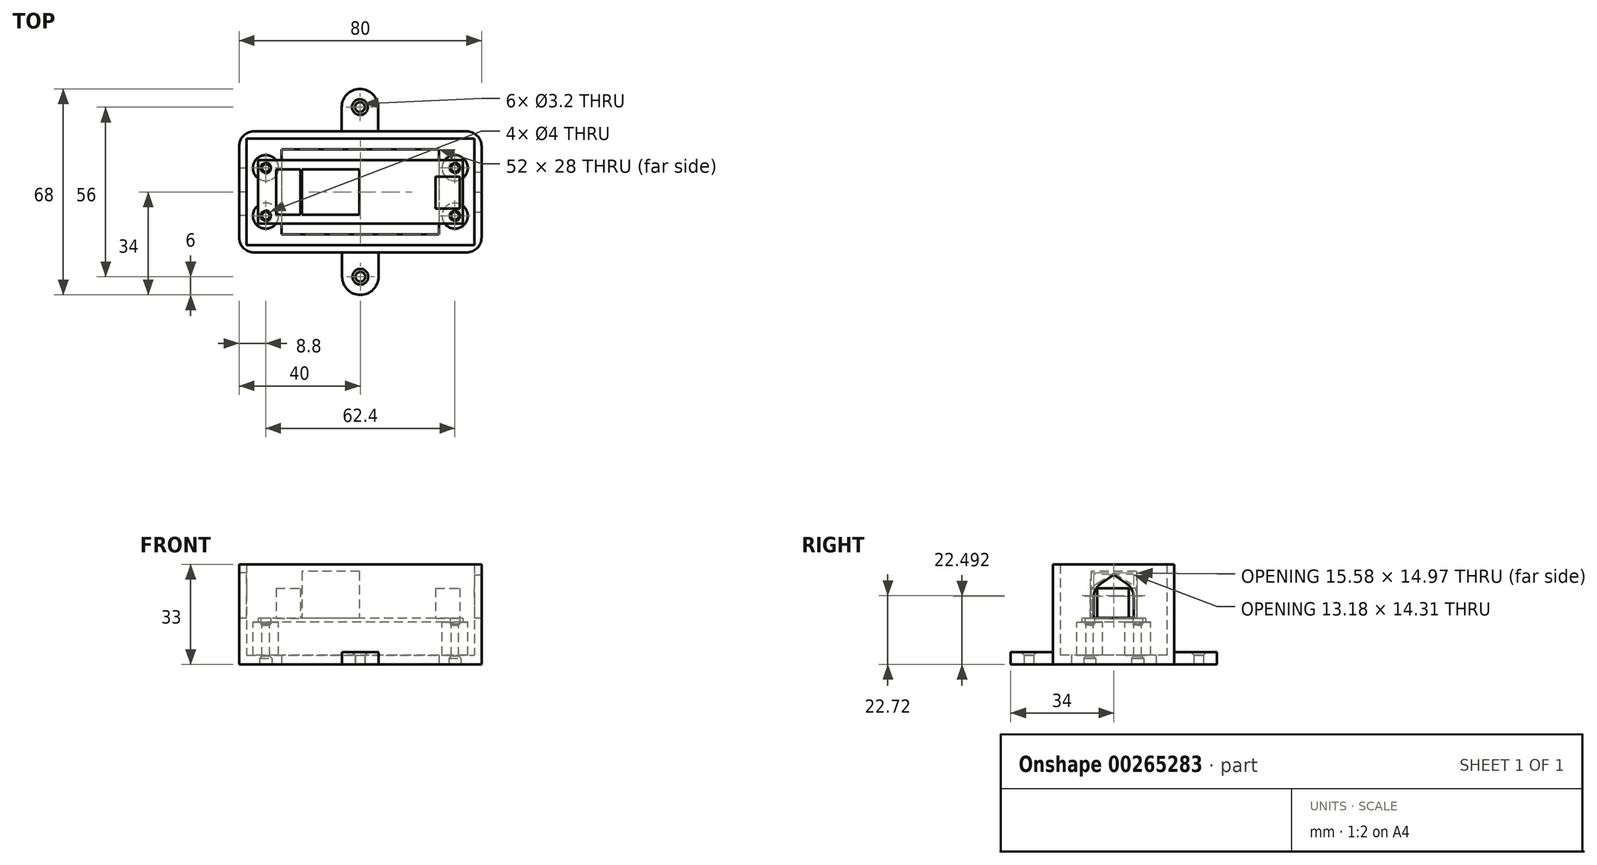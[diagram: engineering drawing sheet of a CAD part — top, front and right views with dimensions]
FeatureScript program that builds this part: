
annotation { "Feature Type Name" : "Feature", "Feature Type Description" : "" }
export const myFeature = defineFeature(function(context is Context, id is Id, definition is map)
    precondition{}
    {
        {
            var Q0;
            Q0=qCreatedBy(makeId("Top.planeOp"),FACE);
            cPlane(context, id + "F0", {"entities" : qUnion([Q0]), "cplaneType" : CPlaneType.OFFSET, "offset" : 14 * mm, "oppositeDirection" : true, "width" : 150 * mm, "height" : 150 * mm});
        }
        {
            var Q0;
            Q0=qCreatedBy(makeId("Top.planeOp"),FACE);
            var sketch = newSketch(context, id + "F1", { "sketchPlane" : qUnion([Q0])});
            skLineSegment(sketch, "E0.bottom", {"start": v(33.8, 10.5) * mm, "end": v(-33.8, 10.5) * mm});
            skLineSegment(sketch, "E0.top", {"start": v(33.8, -10.5) * mm, "end": v(-33.8, -10.5) * mm});
            skLineSegment(sketch, "E0.left", {"start": v(33.8, 10.5) * mm, "end": v(33.8, -10.5) * mm});
            skLineSegment(sketch, "E0.right", {"start": v(-33.8, 10.5) * mm, "end": v(-33.8, -10.5) * mm});
            skPoint(sketch, "E0.middle", {"position": v(0, 0) * mm});
            skCircle(sketch, "E1", {"center": v(-31.2, 7.9) * mm, "radius": 1.6 * mm});
            skCircle(sketch, "E2", {"center": v(31.2, 7.9) * mm, "radius": 1.6 * mm});
            skCircle(sketch, "E3", {"center": v(-31.2, -7.9) * mm, "radius": 1.6 * mm});
            skCircle(sketch, "E4", {"center": v(31.2, -7.9) * mm, "radius": 1.6 * mm});
            skSolve(sketch);
        }
        {
            var Q0;
            Q0 = qSketchRegion(id + "F1", true);
            extrude(context, id + "F2", {"entities" : qUnion([Q0]), "depth" : 1.2 * mm});
        }
        {
            var Q0;
            Q0=qCreatedBy(id+"F0.planeOp",FACE);
            var sketch = newSketch(context, id + "F3", { "sketchPlane" : qUnion([Q0])});
            skLineSegment(sketch, "E5.bottom", {"start": v(-40, 20) * mm, "end": v(40, 20) * mm});
            skLineSegment(sketch, "E5.top", {"start": v(-40, -20) * mm, "end": v(40, -20) * mm});
            skLineSegment(sketch, "E5.left", {"start": v(-40, 20) * mm, "end": v(-40, -20) * mm});
            skLineSegment(sketch, "E5.right", {"start": v(40, 20) * mm, "end": v(40, -20) * mm});
            skPoint(sketch, "E5.middle", {"position": v(0, 0) * mm});
            skLineSegment(sketch, "E6.bottom", {"start": v(26, 14) * mm, "end": v(-26, 14) * mm});
            skLineSegment(sketch, "E6.top", {"start": v(26, -14) * mm, "end": v(-26, -14) * mm});
            skLineSegment(sketch, "E6.left", {"start": v(26, 14) * mm, "end": v(26, -14) * mm});
            skLineSegment(sketch, "E6.right", {"start": v(-26, 14) * mm, "end": v(-26, -14) * mm});
            skSolve(sketch);
        }
        {
            var Q0;
            Q0 = qSketchRegion(id + "F3", true);
            extrude(context, id + "F4", {"entities" : qUnion([Q0]), "depth" : 3 * mm});
        }
        {
            var Q0;
            Q0=makeQuery(id+"F2.opExtrude","CAP_FACE",FACE,{"disambiguationData":[OSD([sQuery(id+"F1.wireOp",EDGE,"E0.bottom"),sQuery(id+"F1.wireOp",EDGE,"E0.top"),sQuery(id+"F1.wireOp",EDGE,"E0.left"),sQuery(id+"F1.wireOp",EDGE,"E0.right"),sQuery(id+"F1.wireOp",EDGE,"E1"),sQuery(id+"F1.wireOp",EDGE,"E2"),sQuery(id+"F1.wireOp",EDGE,"E3"),sQuery(id+"F1.wireOp",EDGE,"E4")])],"isStart":true});
            var sketch = newSketch(context, id + "F5", { "sketchPlane" : qUnion([Q0])});
            skCircle(sketch, "E7", {"center": v(-31.2, 7.9) * mm, "radius": 1.25 * mm});
            skCircle(sketch, "E8", {"center": v(-31.2, 7.9) * mm, "radius": 4.25 * mm});
            skCircle(sketch, "E9", {"center": v(-31.2, -7.9) * mm, "radius": 1.25 * mm});
            skCircle(sketch, "E10", {"center": v(-31.2, -7.9) * mm, "radius": 4.25 * mm});
            skCircle(sketch, "E11", {"center": v(31.2, 7.9) * mm, "radius": 1.25 * mm});
            skCircle(sketch, "E12", {"center": v(31.2, 7.9) * mm, "radius": 4.25 * mm});
            skCircle(sketch, "E13", {"center": v(31.2, -7.9) * mm, "radius": 1.25 * mm});
            skCircle(sketch, "E14", {"center": v(31.2, -7.9) * mm, "radius": 4.25 * mm});
            skSolve(sketch);
        }
        {
            var Q0;
            Q0 = qSketchRegion(id + "F5", true);
            extrude(context, id + "F6", {"entities" : qUnion([Q0]), "operationType" : NewBodyOperationType.ADD, "depth" : 14 * mm});
        }
        {
            var Q0;
            Q0=makeQuery(id+"F2.opExtrude","CAP_FACE",FACE,{"disambiguationData":[OSD([sQuery(id+"F1.wireOp",EDGE,"E0.bottom"),sQuery(id+"F1.wireOp",EDGE,"E0.top"),sQuery(id+"F1.wireOp",EDGE,"E0.left"),sQuery(id+"F1.wireOp",EDGE,"E0.right"),sQuery(id+"F1.wireOp",EDGE,"E1"),sQuery(id+"F1.wireOp",EDGE,"E2"),sQuery(id+"F1.wireOp",EDGE,"E3"),sQuery(id+"F1.wireOp",EDGE,"E4")])],"isStart":false});
            var sketch = newSketch(context, id + "F7", { "sketchPlane" : qUnion([Q0])});
            skLineSegment(sketch, "E15.bottom", {"start": v(-27.8, 7.5) * mm, "end": v(-19.8, 7.5) * mm});
            skLineSegment(sketch, "E15.top", {"start": v(-27.8, -7.5) * mm, "end": v(-19.8, -7.5) * mm});
            skLineSegment(sketch, "E15.left", {"start": v(-27.8, 7.5) * mm, "end": v(-27.8, -7.5) * mm});
            skLineSegment(sketch, "E15.right", {"start": v(-19.8, 7.5) * mm, "end": v(-19.8, -7.5) * mm});
            skLineSegment(sketch, "E16.bottom", {"start": v(24.8, 5) * mm, "end": v(32.8, 5) * mm});
            skLineSegment(sketch, "E16.top", {"start": v(24.8, -5.5) * mm, "end": v(32.8, -5.5) * mm});
            skLineSegment(sketch, "E16.left", {"start": v(24.8, 5) * mm, "end": v(24.8, -5.5) * mm});
            skLineSegment(sketch, "E16.right", {"start": v(32.8, 5) * mm, "end": v(32.8, -5.5) * mm});
            skSolve(sketch);
        }
        {
            var Q0;
            Q0 = qSketchRegion(id + "F7", true);
            extrude(context, id + "F8", {"entities" : qUnion([Q0]), "operationType" : NewBodyOperationType.ADD, "depth" : 10 * mm});
        }
        {
            var Q0;
            Q0=makeQuery(id+"F2.opExtrude","CAP_FACE",FACE,{"disambiguationData":[OSD([sQuery(id+"F1.wireOp",EDGE,"E0.bottom"),sQuery(id+"F1.wireOp",EDGE,"E0.top"),sQuery(id+"F1.wireOp",EDGE,"E0.left"),sQuery(id+"F1.wireOp",EDGE,"E0.right"),sQuery(id+"F1.wireOp",EDGE,"E1"),sQuery(id+"F1.wireOp",EDGE,"E2"),sQuery(id+"F1.wireOp",EDGE,"E3"),sQuery(id+"F1.wireOp",EDGE,"E4")])],"isStart":false});
            var sketch = newSketch(context, id + "F9", { "sketchPlane" : qUnion([Q0])});
            skLineSegment(sketch, "E17.bottom", {"start": v(-0.3, 7.5) * mm, "end": v(-19.3, 7.5) * mm});
            skLineSegment(sketch, "E17.top", {"start": v(-0.3, -7.5) * mm, "end": v(-19.3, -7.5) * mm});
            skLineSegment(sketch, "E17.left", {"start": v(-0.3, 7.5) * mm, "end": v(-0.3, -7.5) * mm});
            skLineSegment(sketch, "E17.right", {"start": v(-19.3, 7.5) * mm, "end": v(-19.3, -7.5) * mm});
            skSolve(sketch);
        }
        {
            var Q0;
            Q0 = qSketchRegion(id + "F9", true);
            extrude(context, id + "F10", {"entities" : qUnion([Q0]), "operationType" : NewBodyOperationType.ADD, "depth" : 15.5 * mm});
        }
        {
            var Q0;
            {var subQ0=sQuery(id+"F3.wireOp",EDGE,"E5.right");var subQ1=sQuery(id+"F3.wireOp",EDGE,"E5.left");var subQ2=sQuery(id+"F3.wireOp",EDGE,"E5.top");var subQ3=sQuery(id+"F3.wireOp",EDGE,"E5.bottom");Q0=makeQuery(id+"F6.boolean.opBoolean","SPLIT",FACE,{"disambiguationData":[TD([makeQuery(id+"F4.opExtrude","SWEPT_FACE",FACE,{"disambiguationData":[OSD([subQ3])]})])],"derivedFrom":makeQuery(id+"F4.opExtrude","CAP_FACE",FACE,{"disambiguationData":[OSD([subQ3,subQ2,subQ1,subQ0])],"isStart":false})});}
            var sketch = newSketch(context, id + "F11", { "sketchPlane" : qUnion([Q0])});
            skLineSegment(sketch, "E18.bottom", {"start": v(-40, 20) * mm, "end": v(40, 20) * mm});
            skLineSegment(sketch, "E18.top", {"start": v(-40, -20) * mm, "end": v(40, -20) * mm});
            skLineSegment(sketch, "E18.left", {"start": v(-40, 20) * mm, "end": v(-40, -20) * mm});
            skLineSegment(sketch, "E18.right", {"start": v(40, 20) * mm, "end": v(40, -20) * mm});
            skPoint(sketch, "E18.middle", {"position": v(0, 0) * mm});
            skLineSegment(sketch, "E19.bottom", {"start": v(-37.6, 17.6) * mm, "end": v(37.6, 17.6) * mm});
            skLineSegment(sketch, "E19.top", {"start": v(-37.6, -17.6) * mm, "end": v(37.6, -17.6) * mm});
            skLineSegment(sketch, "E19.left", {"start": v(-37.6, 17.6) * mm, "end": v(-37.6, -17.6) * mm});
            skLineSegment(sketch, "E19.right", {"start": v(37.6, 17.6) * mm, "end": v(37.6, -17.6) * mm});
            skSolve(sketch);
        }
        {
            var Q0;
            Q0 = qSketchRegion(id + "F11", true);
            extrude(context, id + "F12", {"entities" : qUnion([Q0]), "operationType" : NewBodyOperationType.ADD, "depth" : 30 * mm});
        }
        {
            var Q0;
            Q0=makeQuery(id+"F12.boolean.opBoolean","MERGE",FACE,{"derivedFrom":[makeQuery(id+"F4.opExtrude","SWEPT_FACE",FACE,{"disambiguationData":[OSD([sQuery(id+"F3.wireOp",EDGE,"E5.left")])]}),makeQuery(id+"F12.opExtrude","SWEPT_FACE",FACE,{"disambiguationData":[OSD([sQuery(id+"F11.wireOp",EDGE,"E18.left")])]})]});
            var sketch = newSketch(context, id + "F13", { "sketchPlane" : qUnion([Q0])});
            skLineSegment(sketch, "E20.bottom", {"start": v(7.79, 1.23) * mm, "end": v(-7.79, 1.23) * mm});
            skLineSegment(sketch, "E20.left", {"start": v(7.79, 1.23) * mm, "end": v(7.79, 11.29) * mm});
            skLineSegment(sketch, "E20.right", {"start": v(-7.79, 1.23) * mm, "end": v(-7.79, 11.29) * mm});
            skPoint(sketch, "E20.middle", {"position": v(0, 6.26) * mm});
            skLineSegment(sketch, "E21", {"start": v(7.79, 11.29) * mm, "end": v(0, 16.2) * mm});
            skLineSegment(sketch, "E22", {"start": v(0, 16.2) * mm, "end": v(-7.79, 11.29) * mm});
            skSolve(sketch);
        }
        {
            var Q0;
            Q0 = qSketchRegion(id + "F13", true);
            var Q1;
            Q1=makeQuery(id+"F12.opExtrude","SWEPT_FACE",FACE,{"disambiguationData":[OSD([sQuery(id+"F11.wireOp",EDGE,"E19.left")])]});
            extrude(context, id + "F14", {"entities" : qUnion([Q0]), "operationType" : NewBodyOperationType.REMOVE, "endBound" : BoundingType.UP_TO_SURFACE, "oppositeDirection" : true, "endBoundEntityFace" : qUnion([Q1]), "depth" : 25 * mm});
        }
        {
            var Q0;
            Q0=makeQuery(id+"F12.boolean.opBoolean","MERGE",FACE,{"derivedFrom":[makeQuery(id+"F4.opExtrude","SWEPT_FACE",FACE,{"disambiguationData":[OSD([sQuery(id+"F3.wireOp",EDGE,"E5.right")])]}),makeQuery(id+"F12.opExtrude","SWEPT_FACE",FACE,{"disambiguationData":[OSD([sQuery(id+"F11.wireOp",EDGE,"E18.right")])]})]});
            var sketch = newSketch(context, id + "F15", { "sketchPlane" : qUnion([Q0])});
            skLineSegment(sketch, "E23.bottom", {"start": v(6.6, 1.33) * mm, "end": v(-6.6, 1.33) * mm});
            skLineSegment(sketch, "E23.left", {"start": v(6.6, 1.33) * mm, "end": v(6.6, 10.98) * mm});
            skLineSegment(sketch, "E23.right", {"start": v(-6.6, 1.33) * mm, "end": v(-6.6, 10.98) * mm});
            skPoint(sketch, "E23.middle", {"position": v(0, 6.16) * mm});
            skLineSegment(sketch, "E24", {"start": v(6.6, 10.98) * mm, "end": v(0, 15.65) * mm});
            skLineSegment(sketch, "E25", {"start": v(0, 15.65) * mm, "end": v(-6.6, 10.98) * mm});
            skSolve(sketch);
        }
        {
            var Q0;
            Q0 = qSketchRegion(id + "F15", true);
            var Q1;
            Q1=makeQuery(id+"F12.opExtrude","SWEPT_FACE",FACE,{"disambiguationData":[OSD([sQuery(id+"F11.wireOp",EDGE,"E19.right")])]});
            extrude(context, id + "F16", {"entities" : qUnion([Q0]), "operationType" : NewBodyOperationType.REMOVE, "endBound" : BoundingType.UP_TO_SURFACE, "oppositeDirection" : true, "endBoundEntityFace" : qUnion([Q1]), "depth" : 25 * mm});
        }
        {
            var Q0;
            Q0=makeQuery(id+"F16.boolean.opBoolean","COPY",EDGE,{"derivedFrom":makeQuery(id+"F16.opExtrude","SWEPT_EDGE",EDGE,{"disambiguationData":[OSD([sQuery(id+"F15.wireOp",EDGE,"E23.left"),sQuery(id+"F15.wireOp",EDGE,"E24")])]})});
            var Q1;
            Q1=makeQuery(id+"F14.boolean.opBoolean","COPY",EDGE,{"derivedFrom":makeQuery(id+"F14.opExtrude","SWEPT_EDGE",EDGE,{"disambiguationData":[OSD([sQuery(id+"F13.wireOp",EDGE,"E20.left"),sQuery(id+"F13.wireOp",EDGE,"E21")])]})});
            var Q2;
            Q2=makeQuery(id+"F14.boolean.opBoolean","COPY",EDGE,{"derivedFrom":makeQuery(id+"F14.opExtrude","SWEPT_EDGE",EDGE,{"disambiguationData":[OSD([sQuery(id+"F13.wireOp",EDGE,"E20.right"),sQuery(id+"F13.wireOp",EDGE,"E22")])]})});
            var Q3;
            Q3=makeQuery(id+"F16.boolean.opBoolean","COPY",EDGE,{"derivedFrom":makeQuery(id+"F16.opExtrude","SWEPT_EDGE",EDGE,{"disambiguationData":[OSD([sQuery(id+"F15.wireOp",EDGE,"E23.right"),sQuery(id+"F15.wireOp",EDGE,"E25")])]})});
            var Q4;
            Q4=makeQuery(id+"F12.boolean.opBoolean","MERGE",EDGE,{"derivedFrom":[makeQuery(id+"F4.opExtrude","SWEPT_EDGE",EDGE,{"disambiguationData":[OSD([sQuery(id+"F3.wireOp",EDGE,"E5.top"),sQuery(id+"F3.wireOp",EDGE,"E5.right")])]}),makeQuery(id+"F12.opExtrude","SWEPT_EDGE",EDGE,{"disambiguationData":[OSD([sQuery(id+"F11.wireOp",EDGE,"E18.top"),sQuery(id+"F11.wireOp",EDGE,"E18.right")])]})]});
            var Q5;
            Q5=makeQuery(id+"F12.boolean.opBoolean","MERGE",EDGE,{"derivedFrom":[makeQuery(id+"F4.opExtrude","SWEPT_EDGE",EDGE,{"disambiguationData":[OSD([sQuery(id+"F3.wireOp",EDGE,"E5.bottom"),sQuery(id+"F3.wireOp",EDGE,"E5.right")])]}),makeQuery(id+"F12.opExtrude","SWEPT_EDGE",EDGE,{"disambiguationData":[OSD([sQuery(id+"F11.wireOp",EDGE,"E18.bottom"),sQuery(id+"F11.wireOp",EDGE,"E18.right")])]})]});
            var Q6;
            Q6=makeQuery(id+"F12.boolean.opBoolean","MERGE",EDGE,{"derivedFrom":[makeQuery(id+"F4.opExtrude","SWEPT_EDGE",EDGE,{"disambiguationData":[OSD([sQuery(id+"F3.wireOp",EDGE,"E5.bottom"),sQuery(id+"F3.wireOp",EDGE,"E5.left")])]}),makeQuery(id+"F12.opExtrude","SWEPT_EDGE",EDGE,{"disambiguationData":[OSD([sQuery(id+"F11.wireOp",EDGE,"E18.bottom"),sQuery(id+"F11.wireOp",EDGE,"E18.left")])]})]});
            var Q7;
            Q7=makeQuery(id+"F12.boolean.opBoolean","MERGE",EDGE,{"derivedFrom":[makeQuery(id+"F4.opExtrude","SWEPT_EDGE",EDGE,{"disambiguationData":[OSD([sQuery(id+"F3.wireOp",EDGE,"E5.top"),sQuery(id+"F3.wireOp",EDGE,"E5.left")])]}),makeQuery(id+"F12.opExtrude","SWEPT_EDGE",EDGE,{"disambiguationData":[OSD([sQuery(id+"F11.wireOp",EDGE,"E18.top"),sQuery(id+"F11.wireOp",EDGE,"E18.left")])]})]});
            fillet(context, id + "F17", {"entities" : qUnion([Q0, Q1, Q2, Q3, Q4, Q5, Q6, Q7]), "radius" : 5 * mm, "tangentPropagation" : true, "allowEdgeOverflow" : false});
        }
        {
            var Q0;
            Q0=makeQuery(id+"F4.opExtrude","CAP_FACE",FACE,{"disambiguationData":[OSD([sQuery(id+"F3.wireOp",EDGE,"E5.bottom"),sQuery(id+"F3.wireOp",EDGE,"E5.top"),sQuery(id+"F3.wireOp",EDGE,"E5.left"),sQuery(id+"F3.wireOp",EDGE,"E5.right"),sQuery(id+"F3.wireOp",EDGE,"E6.bottom"),sQuery(id+"F3.wireOp",EDGE,"E6.top"),sQuery(id+"F3.wireOp",EDGE,"E6.left"),sQuery(id+"F3.wireOp",EDGE,"E6.right")])],"isStart":true});
            var sketch = newSketch(context, id + "F18", { "sketchPlane" : qUnion([Q0])});
            skLineSegment(sketch, "E26.bottom", {"start": v(6, 34) * mm, "end": v(-6, 34) * mm});
            skLineSegment(sketch, "E26.top", {"start": v(6, 20) * mm, "end": v(-6, 20) * mm});
            skLineSegment(sketch, "E26.left", {"start": v(6, 34) * mm, "end": v(6, 20) * mm});
            skLineSegment(sketch, "E26.right", {"start": v(-6, 34) * mm, "end": v(-6, 20) * mm});
            skPoint(sketch, "E26.middle", {"position": v(0, 28) * mm});
            skCircle(sketch, "E27", {"center": v(0, 28) * mm, "radius": 1.6 * mm});
            skLineSegment(sketch, "E28.bottom", {"start": v(5.85, -20) * mm, "end": v(-6.15, -20) * mm});
            skLineSegment(sketch, "E28.top", {"start": v(5.85, -34) * mm, "end": v(-6.15, -34) * mm});
            skLineSegment(sketch, "E28.left", {"start": v(5.85, -20) * mm, "end": v(5.85, -34) * mm});
            skLineSegment(sketch, "E28.right", {"start": v(-6.15, -20) * mm, "end": v(-6.15, -34) * mm});
            skPoint(sketch, "E28.middle", {"position": v(-0.15, -28) * mm});
            skCircle(sketch, "E29", {"center": v(-0.15, -28) * mm, "radius": 1.6 * mm});
            skSolve(sketch);
        }
        {
            var Q0;
            Q0 = qSketchRegion(id + "F18", true);
            extrude(context, id + "F19", {"entities" : qUnion([Q0]), "operationType" : NewBodyOperationType.ADD, "oppositeDirection" : true, "depth" : 4 * mm});
        }
        {
            var Q0;
            Q0=makeQuery(id+"F19.opExtrude","SWEPT_EDGE",EDGE,{"disambiguationData":[OSD([sQuery(id+"F18.wireOp",EDGE,"E26.bottom"),sQuery(id+"F18.wireOp",EDGE,"E26.left")])]});
            var Q1;
            Q1=makeQuery(id+"F19.opExtrude","SWEPT_EDGE",EDGE,{"disambiguationData":[OSD([sQuery(id+"F18.wireOp",EDGE,"E26.bottom"),sQuery(id+"F18.wireOp",EDGE,"E26.right")])]});
            var Q2;
            Q2=makeQuery(id+"F19.opExtrude","SWEPT_EDGE",EDGE,{"disambiguationData":[OSD([sQuery(id+"F18.wireOp",EDGE,"E28.top"),sQuery(id+"F18.wireOp",EDGE,"E28.left")])]});
            var Q3;
            Q3=makeQuery(id+"F19.opExtrude","SWEPT_EDGE",EDGE,{"disambiguationData":[OSD([sQuery(id+"F18.wireOp",EDGE,"E28.top"),sQuery(id+"F18.wireOp",EDGE,"E28.right")])]});
            var Q4;
            Q4=makeQuery(id+"F19.opExtrude","SWEPT_EDGE",EDGE,{"disambiguationData":[OSD([sQuery(id+"F3.wireOp",EDGE,"E5.bottom"),sQuery(id+"F18.wireOp",EDGE,"E28.bottom"),sQuery(id+"F18.wireOp",EDGE,"E28.left")])]});
            var Q5;
            Q5=makeQuery(id+"F19.opExtrude","SWEPT_EDGE",EDGE,{"disambiguationData":[OSD([sQuery(id+"F3.wireOp",EDGE,"E5.bottom"),sQuery(id+"F18.wireOp",EDGE,"E28.bottom"),sQuery(id+"F18.wireOp",EDGE,"E28.right")])]});
            var Q6;
            Q6=makeQuery(id+"F19.opExtrude","SWEPT_EDGE",EDGE,{"disambiguationData":[OSD([sQuery(id+"F3.wireOp",EDGE,"E5.top"),sQuery(id+"F18.wireOp",EDGE,"E26.top"),sQuery(id+"F18.wireOp",EDGE,"E26.left")])]});
            var Q7;
            Q7=makeQuery(id+"F19.opExtrude","SWEPT_EDGE",EDGE,{"disambiguationData":[OSD([sQuery(id+"F3.wireOp",EDGE,"E5.top"),sQuery(id+"F18.wireOp",EDGE,"E26.top"),sQuery(id+"F18.wireOp",EDGE,"E26.right")])]});
            fillet(context, id + "F20", {"entities" : qUnion([Q0, Q1, Q2, Q3, Q4, Q5, Q6, Q7]), "radius" : 6 * mm, "tangentPropagation" : true, "allowEdgeOverflow" : false});
        }
        {
            var Q0;
            Q0=makeQuery(id+"F19.boolean.opBoolean","MERGE",FACE,{"derivedFrom":[makeQuery(id+"F4.opExtrude","CAP_FACE",FACE,{"disambiguationData":[OSD([sQuery(id+"F3.wireOp",EDGE,"E5.bottom"),sQuery(id+"F3.wireOp",EDGE,"E5.top"),sQuery(id+"F3.wireOp",EDGE,"E5.left"),sQuery(id+"F3.wireOp",EDGE,"E5.right"),sQuery(id+"F3.wireOp",EDGE,"E6.bottom"),sQuery(id+"F3.wireOp",EDGE,"E6.top"),sQuery(id+"F3.wireOp",EDGE,"E6.left"),sQuery(id+"F3.wireOp",EDGE,"E6.right")])],"isStart":true}),makeQuery(id+"F19.opExtrude","CAP_FACE",FACE,{"disambiguationData":[OSD([sQuery(id+"F18.wireOp",EDGE,"E26.bottom"),sQuery(id+"F18.wireOp",EDGE,"E26.top"),sQuery(id+"F18.wireOp",EDGE,"E26.left"),sQuery(id+"F18.wireOp",EDGE,"E26.right"),sQuery(id+"F18.wireOp",EDGE,"E27")])],"isStart":true}),makeQuery(id+"F19.opExtrude","CAP_FACE",FACE,{"disambiguationData":[OSD([sQuery(id+"F18.wireOp",EDGE,"E28.bottom"),sQuery(id+"F18.wireOp",EDGE,"E28.top"),sQuery(id+"F18.wireOp",EDGE,"E28.left"),sQuery(id+"F18.wireOp",EDGE,"E28.right"),sQuery(id+"F18.wireOp",EDGE,"E29")])],"isStart":true})]});
            var sketch = newSketch(context, id + "F21", { "sketchPlane" : qUnion([Q0])});
            skCircle(sketch, "E30", {"center": v(-31.2, -7.9) * mm, "radius": 2 * mm});
            skCircle(sketch, "E31", {"center": v(-31.2, 7.9) * mm, "radius": 2 * mm});
            skCircle(sketch, "E32", {"center": v(31.2, -7.9) * mm, "radius": 2 * mm});
            skCircle(sketch, "E33", {"center": v(31.2, 7.9) * mm, "radius": 2 * mm});
            skSolve(sketch);
        }
        {
            var Q0;
            Q0 = qSketchRegion(id + "F21", true);
            extrude(context, id + "F22", {"entities" : qUnion([Q0]), "operationType" : NewBodyOperationType.REMOVE, "oppositeDirection" : true, "depth" : 3 * mm});
        }
        {
            var Q0;
            Q0=makeQuery(id+"F22.boolean.opBoolean","COPY",EDGE,{"derivedFrom":makeQuery(id+"F22.opExtrude","CAP_EDGE",EDGE,{"disambiguationData":[OSD([sQuery(id+"F21.wireOp",EDGE,"E32")])],"isStart":false})});
            var Q1;
            Q1=makeQuery(id+"F22.boolean.opBoolean","COPY",EDGE,{"derivedFrom":makeQuery(id+"F22.opExtrude","CAP_EDGE",EDGE,{"disambiguationData":[OSD([sQuery(id+"F21.wireOp",EDGE,"E33")])],"isStart":false})});
            var Q2;
            Q2=makeQuery(id+"F22.boolean.opBoolean","COPY",EDGE,{"derivedFrom":makeQuery(id+"F22.opExtrude","CAP_EDGE",EDGE,{"disambiguationData":[OSD([sQuery(id+"F21.wireOp",EDGE,"E31")])],"isStart":false})});
            var Q3;
            Q3=makeQuery(id+"F22.boolean.opBoolean","COPY",EDGE,{"derivedFrom":makeQuery(id+"F22.opExtrude","CAP_EDGE",EDGE,{"disambiguationData":[OSD([sQuery(id+"F21.wireOp",EDGE,"E30")])],"isStart":false})});
            var Q4;
            Q4=makeQuery(id+"F6.opExtrude","CAP_EDGE",EDGE,{"disambiguationData":[OSD([sQuery(id+"F5.wireOp",EDGE,"E7")])],"isStart":true});
            var Q5;
            Q5=makeQuery(id+"F6.opExtrude","CAP_EDGE",EDGE,{"disambiguationData":[OSD([sQuery(id+"F5.wireOp",EDGE,"E9")])],"isStart":true});
            var Q6;
            Q6=makeQuery(id+"F6.opExtrude","CAP_EDGE",EDGE,{"disambiguationData":[OSD([sQuery(id+"F5.wireOp",EDGE,"E11")])],"isStart":true});
            var Q7;
            Q7=makeQuery(id+"F6.opExtrude","CAP_EDGE",EDGE,{"disambiguationData":[OSD([sQuery(id+"F5.wireOp",EDGE,"E13")])],"isStart":true});
            var Q8;
            Q8=makeQuery(id+"F19.opExtrude","CAP_EDGE",EDGE,{"disambiguationData":[OSD([sQuery(id+"F18.wireOp",EDGE,"E27")])],"isStart":false});
            var Q9;
            Q9=makeQuery(id+"F19.opExtrude","CAP_EDGE",EDGE,{"disambiguationData":[OSD([sQuery(id+"F18.wireOp",EDGE,"E29")])],"isStart":false});
            chamfer(context, id + "F23", {"entities" : qUnion([Q0, Q1, Q2, Q3, Q4, Q5, Q6, Q7, Q8, Q9]), "width" : 1 * mm, "tangentPropagation" : true});
        }
    });
